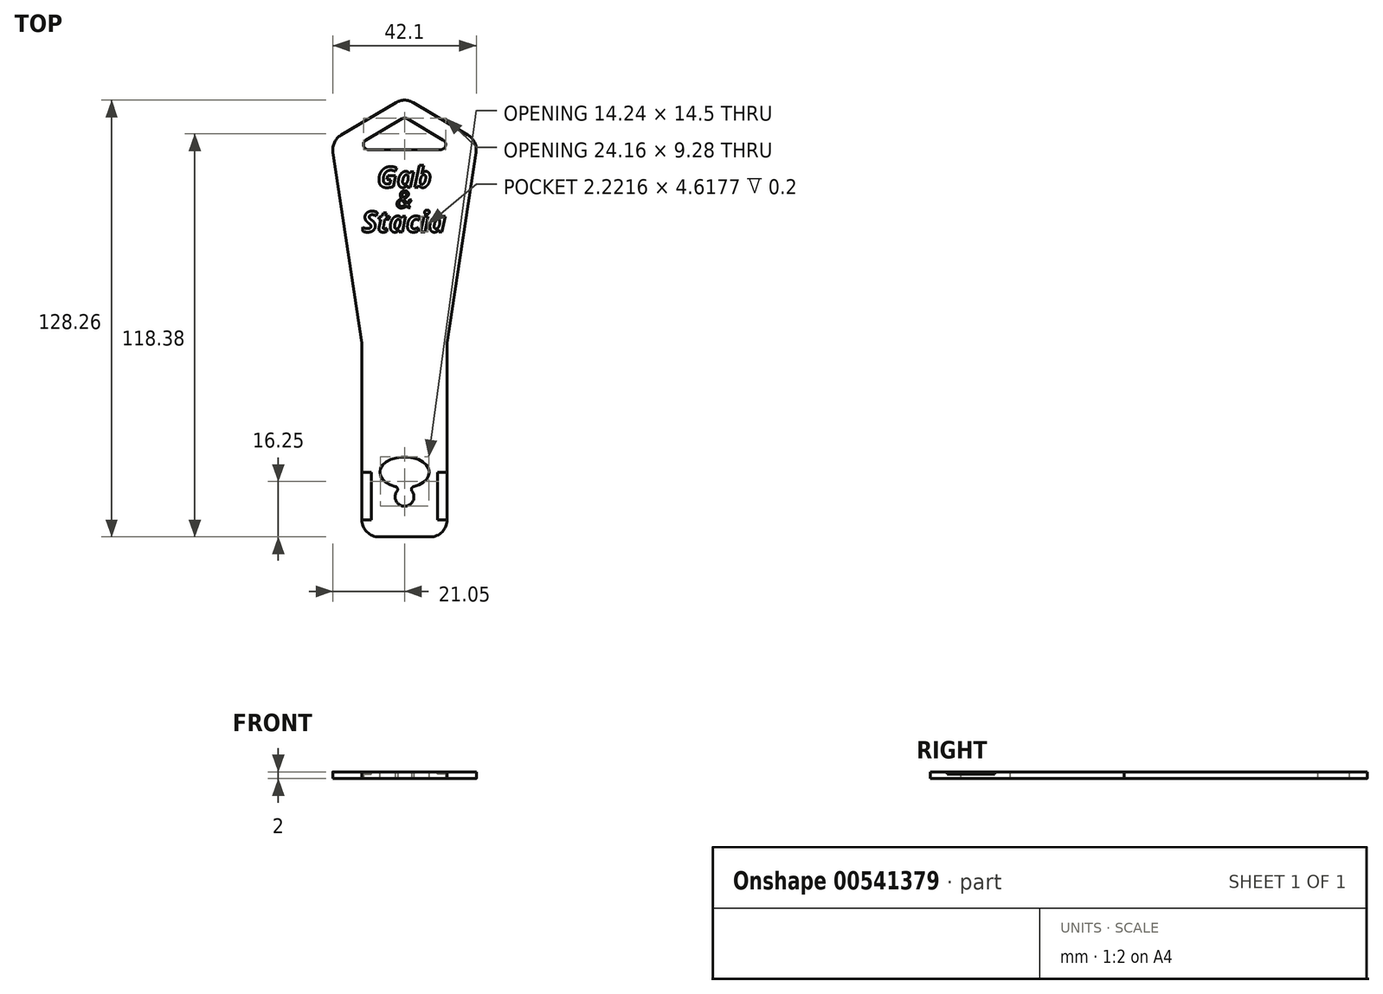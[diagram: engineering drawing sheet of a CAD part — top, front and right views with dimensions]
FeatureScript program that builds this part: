
annotation { "Feature Type Name" : "Feature", "Feature Type Description" : "" }
export const myFeature = defineFeature(function(context is Context, id is Id, definition is map)
    precondition{}
    {
        {
            var Q0;
            Q0=qCreatedBy(makeId("Top.planeOp"),FACE);
            var sketch = newSketch(context, id + "F0", { "sketchPlane" : qUnion([Q0])});
            skLineSegment(sketch, "E0", {"start": v(0, -57) * mm, "end": v(-7.5, -57) * mm});
            skLineSegment(sketch, "E1", {"start": v(-12.5, -52) * mm, "end": v(-12.5, 0) * mm});
            skLineSegment(sketch, "E2", {"start": v(-12.5, 0) * mm, "end": v(-21, 56) * mm});
            skLineSegment(sketch, "E3", {"start": v(-18.6, 61.04) * mm, "end": v(-2.55, 70.56) * mm});
            skLineSegment(sketch, "E4.0", {"start": v(-11.35, 59.53) * mm, "end": v(-0.77, 65.81) * mm});
            skLineSegment(sketch, "E4.1", {"start": v(-7.44, 0) * mm, "end": v(-16.05, 56.74) * mm, "construction": true});
            skLineSegment(sketch, "E5", {"start": v(-10.58, 56.74) * mm, "end": v(0, 56.74) * mm});
            skPoint(sketch, "E6.visualSharp", {"position": v(-21.5, 59.32) * mm});
            skArc(sketch, "E6.filletArc", {"start": v(-18.6, 61.04) * mm, "mid": v(-20.57, 58.88) * mm, "end": v(-21, 56) * mm});
            skPoint(sketch, "E7.visualSharp", {"position": v(-12.5, -57) * mm});
            skArc(sketch, "E7.filletArc", {"start": v(-12.5, -52) * mm, "mid": v(-11.04, -55.54) * mm, "end": v(-7.5, -57) * mm});
            skArc(sketch, "E8.filletArc", {"start": v(-11.35, 59.53) * mm, "mid": v(-12.03, 57.84) * mm, "end": v(-10.58, 56.74) * mm});
            skLineSegment(sketch, "E9.MirrorCS", {"start": v(11.35, 59.53) * mm, "end": v(0.77, 65.81) * mm});
            skArc(sketch, "E10.MirrorCS", {"start": v(11.35, 59.53) * mm, "mid": v(12.03, 57.84) * mm, "end": v(10.58, 56.74) * mm});
            skLineSegment(sketch, "E11.MirrorCS", {"start": v(10.58, 56.74) * mm, "end": v(0, 56.74) * mm});
            skLineSegment(sketch, "E12.MirrorCS", {"start": v(18.6, 61.04) * mm, "end": v(2.55, 70.56) * mm});
            skArc(sketch, "E13.MirrorCS", {"start": v(18.6, 61.04) * mm, "mid": v(20.57, 58.88) * mm, "end": v(21, 56) * mm});
            skLineSegment(sketch, "E14.MirrorCS", {"start": v(12.5, 0) * mm, "end": v(21, 56) * mm});
            skLineSegment(sketch, "E15.MirrorCS", {"start": v(12.5, -52) * mm, "end": v(12.5, 0) * mm});
            skArc(sketch, "E16.MirrorCS", {"start": v(12.5, -52) * mm, "mid": v(11.04, -55.54) * mm, "end": v(7.5, -57) * mm});
            skLineSegment(sketch, "E17.MirrorCS", {"start": v(0, -57) * mm, "end": v(7.5, -57) * mm});
            skPoint(sketch, "E18.visualSharp", {"position": v(0, 72.08) * mm});
            skArc(sketch, "E18.filletArc", {"start": v(2.55, 70.56) * mm, "mid": v(0, 71.26) * mm, "end": v(-2.55, 70.56) * mm});
            skArc(sketch, "E19.filletArc", {"start": v(0.77, 65.81) * mm, "mid": v(0, 66.02) * mm, "end": v(-0.77, 65.81) * mm});
            skPoint(sketch, "E20", {"position": v(0, -42.5) * mm});
            skArc(sketch, "E21", {"start": v(2.2, -43.6) * mm, "mid": v(2.06, -42.75) * mm, "end": v(2.7, -42.18) * mm});
            skArc(sketch, "E22.MirrorCS", {"start": v(-2.2, -43.6) * mm, "mid": v(-2.06, -42.75) * mm, "end": v(-2.7, -42.18) * mm});
            skEllipticalArc(sketch, "E23", {"construction": true});
            skEllipticalArc(sketch, "E24", {});
            skArc(sketch, "E25", {"start": v(2.2, -43.6) * mm, "mid": v(0, -42.5) * mm, "end": v(-2.2, -43.6) * mm, "construction": true});
            skArc(sketch, "E26", {"start": v(-2.2, -43.6) * mm, "mid": v(0, -48) * mm, "end": v(2.2, -43.6) * mm});
            const initialGuessF0  = {"E23": [0, -0.038, -1, 0, 0.00725, 0.0045, 1.1898007434141231, 1.95179191017567], "E24": [0, -0.038, -1, 0, 0.00725, 0.0045, 1.95179191017567, 1.1898007434141231]};
            skSetInitialGuess(sketch, initialGuessF0);
            skSolve(sketch);
        }
        {
            var Q0;
            Q0 = qSketchRegion(id + "F0", true);
            extrude(context, id + "F1", {"entities" : qUnion([Q0]), "endBound" : BoundingType.SYMMETRIC, "depth" : 2 * mm, "offsetDistance" : 25 * mm});
        }
        {
            var Q0;
            Q0=makeQuery(id+"F1.opExtrude","CAP_FACE",FACE,{"disambiguationData":[OSD([sQuery(id+"F0.wireOp",EDGE,"E0"),sQuery(id+"F0.wireOp",EDGE,"E1"),sQuery(id+"F0.wireOp",EDGE,"E2"),sQuery(id+"F0.wireOp",EDGE,"E3"),sQuery(id+"F0.wireOp",EDGE,"E4.0"),sQuery(id+"F0.wireOp",EDGE,"E5"),sQuery(id+"F0.wireOp",EDGE,"E6.filletArc"),sQuery(id+"F0.wireOp",EDGE,"E7.filletArc"),sQuery(id+"F0.wireOp",EDGE,"E8.filletArc"),sQuery(id+"F0.wireOp",EDGE,"E9.MirrorCS"),sQuery(id+"F0.wireOp",EDGE,"E10.MirrorCS"),sQuery(id+"F0.wireOp",EDGE,"E11.MirrorCS"),sQuery(id+"F0.wireOp",EDGE,"E12.MirrorCS"),sQuery(id+"F0.wireOp",EDGE,"E13.MirrorCS"),sQuery(id+"F0.wireOp",EDGE,"E14.MirrorCS"),sQuery(id+"F0.wireOp",EDGE,"E15.MirrorCS"),sQuery(id+"F0.wireOp",EDGE,"E16.MirrorCS"),sQuery(id+"F0.wireOp",EDGE,"E17.MirrorCS"),sQuery(id+"F0.wireOp",EDGE,"E18.filletArc"),sQuery(id+"F0.wireOp",EDGE,"E19.filletArc"),sQuery(id+"F0.wireOp",EDGE,"E21"),sQuery(id+"F0.wireOp",EDGE,"E22.MirrorCS"),sQuery(id+"F0.wireOp",EDGE,"E24"),sQuery(id+"F0.wireOp",EDGE,"E26")])],"isStart":false});
            var sketch = newSketch(context, id + "F2", { "sketchPlane" : qUnion([Q0])});
            skLineSegment(sketch, "E27.bottom", {"start": v(12.5, -52) * mm, "end": v(9.7, -52) * mm});
            skLineSegment(sketch, "E27.top", {"start": v(12.5, -38) * mm, "end": v(9.7, -38) * mm});
            skLineSegment(sketch, "E27.left", {"start": v(12.5, -52) * mm, "end": v(12.5, -38) * mm});
            skLineSegment(sketch, "E27.right", {"start": v(9.7, -52) * mm, "end": v(9.7, -38) * mm});
            skEllipticalArc(sketch, "E28.0", {});
            skLineSegment(sketch, "E29.MirrorCS", {"start": v(-9.7, -52) * mm, "end": v(-9.7, -38) * mm});
            skLineSegment(sketch, "E30.MirrorCS", {"start": v(-12.5, -52) * mm, "end": v(-9.7, -52) * mm});
            skLineSegment(sketch, "E31.MirrorCS", {"start": v(-12.5, -52) * mm, "end": v(-12.5, -38) * mm});
            skLineSegment(sketch, "E32.MirrorCS", {"start": v(-12.5, -38) * mm, "end": v(-9.7, -38) * mm});
            const initialGuessF2  = {"E28.0": [0, -0.038, -1, 0, 0.00725, 0.0045, 1.91703657235005, 1.224556081239743]};
            skSetInitialGuess(sketch, initialGuessF2);
            skSolve(sketch);
        }
        {
            var Q0;
            Q0 = qSketchRegion(id + "F2", true);
            extrude(context, id + "F3", {"entities" : qUnion([Q0]), "operationType" : NewBodyOperationType.REMOVE, "oppositeDirection" : true, "depth" : (2.2 - 1.5) * mm, "offsetDistance" : 25 * mm});
        }
        {
            var Q0;
            Q0=makeQuery(id+"F1.opExtrude","CAP_FACE",FACE,{"disambiguationData":[OSD([sQuery(id+"F0.wireOp",EDGE,"E0"),sQuery(id+"F0.wireOp",EDGE,"E1"),sQuery(id+"F0.wireOp",EDGE,"E2"),sQuery(id+"F0.wireOp",EDGE,"E3"),sQuery(id+"F0.wireOp",EDGE,"E4.0"),sQuery(id+"F0.wireOp",EDGE,"E5"),sQuery(id+"F0.wireOp",EDGE,"E6.filletArc"),sQuery(id+"F0.wireOp",EDGE,"E7.filletArc"),sQuery(id+"F0.wireOp",EDGE,"E8.filletArc"),sQuery(id+"F0.wireOp",EDGE,"E9.MirrorCS"),sQuery(id+"F0.wireOp",EDGE,"E10.MirrorCS"),sQuery(id+"F0.wireOp",EDGE,"E11.MirrorCS"),sQuery(id+"F0.wireOp",EDGE,"E12.MirrorCS"),sQuery(id+"F0.wireOp",EDGE,"E13.MirrorCS"),sQuery(id+"F0.wireOp",EDGE,"E14.MirrorCS"),sQuery(id+"F0.wireOp",EDGE,"E15.MirrorCS"),sQuery(id+"F0.wireOp",EDGE,"E16.MirrorCS"),sQuery(id+"F0.wireOp",EDGE,"E17.MirrorCS"),sQuery(id+"F0.wireOp",EDGE,"E18.filletArc"),sQuery(id+"F0.wireOp",EDGE,"E19.filletArc"),sQuery(id+"F0.wireOp",EDGE,"E21"),sQuery(id+"F0.wireOp",EDGE,"E22.MirrorCS"),sQuery(id+"F0.wireOp",EDGE,"E24"),sQuery(id+"F0.wireOp",EDGE,"E26")])],"isStart":false});
            var sketch = newSketch(context, id + "F4", { "sketchPlane" : qUnion([Q0])});
            skText(sketch, "E33", { "text": "Gab", "fontName": "NotoSans-BoldItalic.ttf"});
            skText(sketch, "E34", { "text": "&", "fontName": "NotoSans-Italic.ttf"});
            skText(sketch, "E35", { "text": "Stacia", "fontName": "NotoSans-BoldItalic.ttf"});
            const initialGuessF4  = {"E33": [-0.00803, 0.04565, 1, 0, 0.00609], "E34": [-0.00246, 0.03965, 1, 0, 0.005], "E35": [-0.0125, 0.03256, 1, 0, 0.00609]};
            skSetInitialGuess(sketch, initialGuessF4);
            skSolve(sketch);
        }
        {
            var Q0;
            Q0 = qSketchRegion(id + "F4", true);
            extrude(context, id + "F5", {"entities" : qUnion([Q0]), "operationType" : NewBodyOperationType.REMOVE, "oppositeDirection" : true, "depth" : 0.2 * mm, "offsetDistance" : 25 * mm});
        }
    });
